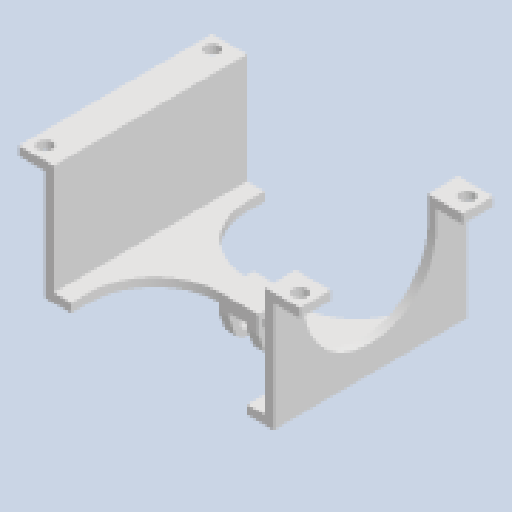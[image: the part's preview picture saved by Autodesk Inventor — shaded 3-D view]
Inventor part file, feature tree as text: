
AUTODESK INVENTOR PART (.ipt)
format: ipt  version: 2025.2 (Build 292293000, 293)  size: 205,312 bytes
history: native  units: mm
features: extrude x5, sketch x5, hole x1, fillet x1
ambient origin geometry x8: Origin, YZ Plane, XZ Plane, XY Plane, X Axis, Y Axis, Z Axis, Center Point
bodies: Solid1 (feature_tree)
feature tree (12):
  extrude  "Extrusion1"  Depth=6.0mm
  hole  "Hole1"  [1 undecoded]
  extrude  "Extrusion2"  Depth=44.0mm
  extrude  "Extrusion3"  Depth=2.0mm
  sketch  "Sketch5"  dims[d11=3.2mm d12=6.0mm d13=4.0mm d14=2.0mm d15=90.0deg d16=8.0mm d17=20.594885mm d18=2.0mm d19=29.0mm d20=21.0mm d21=15.0mm d22=15.0mm d23=0.0mm d24=0.0mm d25=6.0mm d26=19.0mm d27=40.0mm d28=10.0mm d29=0.0mm d30=3.2mm d31=6.0mm d32=4.5mm d33=9.0mm d34=0.0mm d35=4.0mm d36=0.0mm d37=15.0mm]
  extrude  "Extrusion4"  Depth=15.0mm
  extrude  "Extrusion5"  Depth=15.0mm
  fillet  "Fillet1"  Radius=15.0mm
  sketch  "Sketch1"  dims[d0=25.0mm d1=6.0mm]
  sketch  "Sketch2"  dims[d4=2.0mm d5=2.0mm]
  sketch  "Sketch3"  dims[d6=44.0mm d7=0.0mm d8=38.0mm]
  sketch  "Sketch4"  dims[d9=58.0mm]
note: 1 required parameter value undecoded (feature->parameter linkage not recoverable at this tier; creation-order binding heuristic only, values carry confidence <= 0.55)
